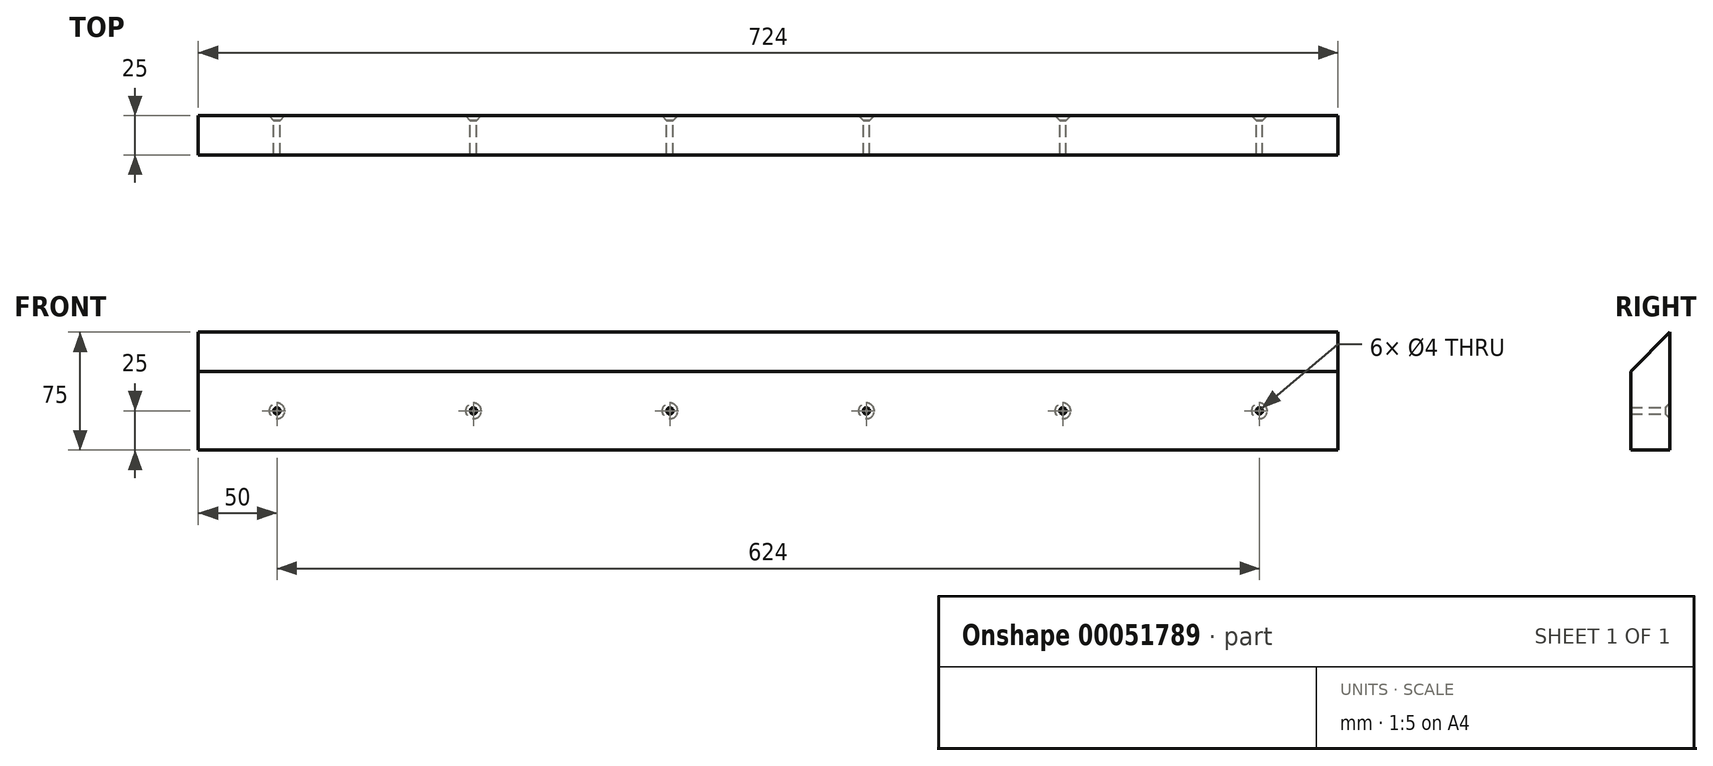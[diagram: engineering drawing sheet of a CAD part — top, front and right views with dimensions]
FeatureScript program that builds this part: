
annotation { "Feature Type Name" : "Feature", "Feature Type Description" : "" }
export const myFeature = defineFeature(function(context is Context, id is Id, definition is map)
    precondition{}
    {
        {
            var Q0;
            Q0=qCreatedBy(makeId("Right.planeOp"),FACE);
            var sketch = newSketch(context, id + "F4", { "sketchPlane" : qUnion([Q0])});
            skLineSegment(sketch, "E0.bottom", {"start": v(-12.5, 37.5) * mm, "end": v(12.5, 37.5) * mm});
            skLineSegment(sketch, "E0.top", {"start": v(-12.5, -37.5) * mm, "end": v(12.5, -37.5) * mm});
            skLineSegment(sketch, "E0.left", {"start": v(-12.5, 37.5) * mm, "end": v(-12.5, -37.5) * mm});
            skLineSegment(sketch, "E0.right", {"start": v(12.5, 37.5) * mm, "end": v(12.5, -37.5) * mm});
            skSolve(sketch);
        }
        {
            var Q0;
            Q0=makeQuery(id+"F4.imprint","IMPRINT",FACE,{"disambiguationData":[TD([[makeQuery(id+"F4.imprint","IMPRINT",EDGE,{"derivedFrom":sQuery(id+"F4.wireOp",EDGE,"E0.bottom")}),-1.0]])]});
            extrude(context, id + "F0", {"entities" : qUnion([Q0]), "depth" : 724 * mm});
        }
        {
            var Q0;
            Q0=makeQuery(id+"F0.opExtrude","SWEPT_EDGE",EDGE,{"disambiguationData":[OSD([sQuery(id+"F4.wireOp",EDGE,"E0.bottom"),sQuery(id+"F4.wireOp",EDGE,"E0.left")])]});
            chamfer(context, id + "F1", {"entities" : qUnion([Q0]), "width" : 25 * mm, "tangentPropagation" : true});
        }
        {
            var Q0;
            Q0=makeQuery(id+"F0.opExtrude","SWEPT_FACE",FACE,{"disambiguationData":[OSD([sQuery(id+"F4.wireOp",EDGE,"E0.right")])]});
            var sketch = newSketch(context, id + "F2", { "sketchPlane" : qUnion([Q0])});
            skPoint(sketch, "E1", {"position": v(-674, -12.5) * mm});
            skPoint(sketch, "E2", {"position": v(324.4, -12.5) * mm});
            skPoint(sketch, "E3", {"position": v(-174.8, -12.5) * mm});
            skPoint(sketch, "E4", {"position": v(-299.6, -12.5) * mm});
            skPoint(sketch, "E5", {"position": v(-50, -12.5) * mm});
            skLineSegment(sketch, "E6", {"start": v(324.4, -12.5) * mm, "end": v(-674, -12.5) * mm, "construction": true});
            skPoint(sketch, "E7", {"position": v(-424.4, -12.5) * mm});
            skPoint(sketch, "E8", {"position": v(-549.2, -12.5) * mm});
            skSolve(sketch);
        }
        {
            var Q0;
            Q0=sQuery(id+"FzWUqEcuTcPPHqZrc_1.wireOp",VERTEX,"fd80adc9-1ce2-4584-9a5b-7f1a8feb4c32");
            var Q1;
            Q1=sQuery(id+"FzWUqEcuTcPPHqZrc_1.wireOp",VERTEX,"2e63b096-3375-4835-bd8d-04c989a85ea9");
            var Q2;
            Q2=sQuery(id+"FzWUqEcuTcPPHqZrc_1.wireOp",VERTEX,"7db0a35c-e0db-47e8-947e-125c11be6248");
            var Q3;
            Q3=sQuery(id+"FzWUqEcuTcPPHqZrc_1.wireOp",VERTEX,"31b235d4-92a0-4b1d-b33a-165163fadd93");
            var Q4;
            Q4=sQuery(id+"FzWUqEcuTcPPHqZrc_1.wireOp",VERTEX,"875cf19a-d195-4894-ae80-60f4e289b197");
            var Q5;
            Q5=sQuery(id+"FzWUqEcuTcPPHqZrc_1.wireOp",VERTEX,"e0710a5b-ccf1-4059-819d-6540484e9a8e");
            var Q6;
            Q6=sQuery(id+"F2.wireOp",VERTEX,"E5");
            var Q7;
            Q7=sQuery(id+"F2.wireOp",VERTEX,"E3");
            var Q8;
            Q8=sQuery(id+"F2.wireOp",VERTEX,"E4");
            var Q9;
            Q9=sQuery(id+"F2.wireOp",VERTEX,"E7");
            var Q10;
            Q10=sQuery(id+"F2.wireOp",VERTEX,"E8");
            var Q11;
            Q11=sQuery(id+"F2.wireOp",VERTEX,"E1");
            var Q12;
            Q12=makeQuery(id+"F0.opExtrude","SWEPT_BODY",BODY,{"disambiguationData":[OSD([sQuery(id+"F4.wireOp",EDGE,"E0.bottom"),sQuery(id+"F4.wireOp",EDGE,"E0.top"),sQuery(id+"F4.wireOp",EDGE,"E0.left"),sQuery(id+"F4.wireOp",EDGE,"E0.right")])]});
            hole(context, id + "F3", {"style" : HoleStyle.C_SINK, "holeDiameter" : 4 * mm, "cSinkDiameter" : 10 * mm, "endStyle" : HoleEndStyle.THROUGH, "locations" : qUnion([Q0, Q1, Q2, Q3, Q4, Q5, Q6, Q7, Q8, Q9, Q10, Q11]), "scope" : qUnion([Q12]), "cSinkAngle" : 90 * degree});
        }
    });
